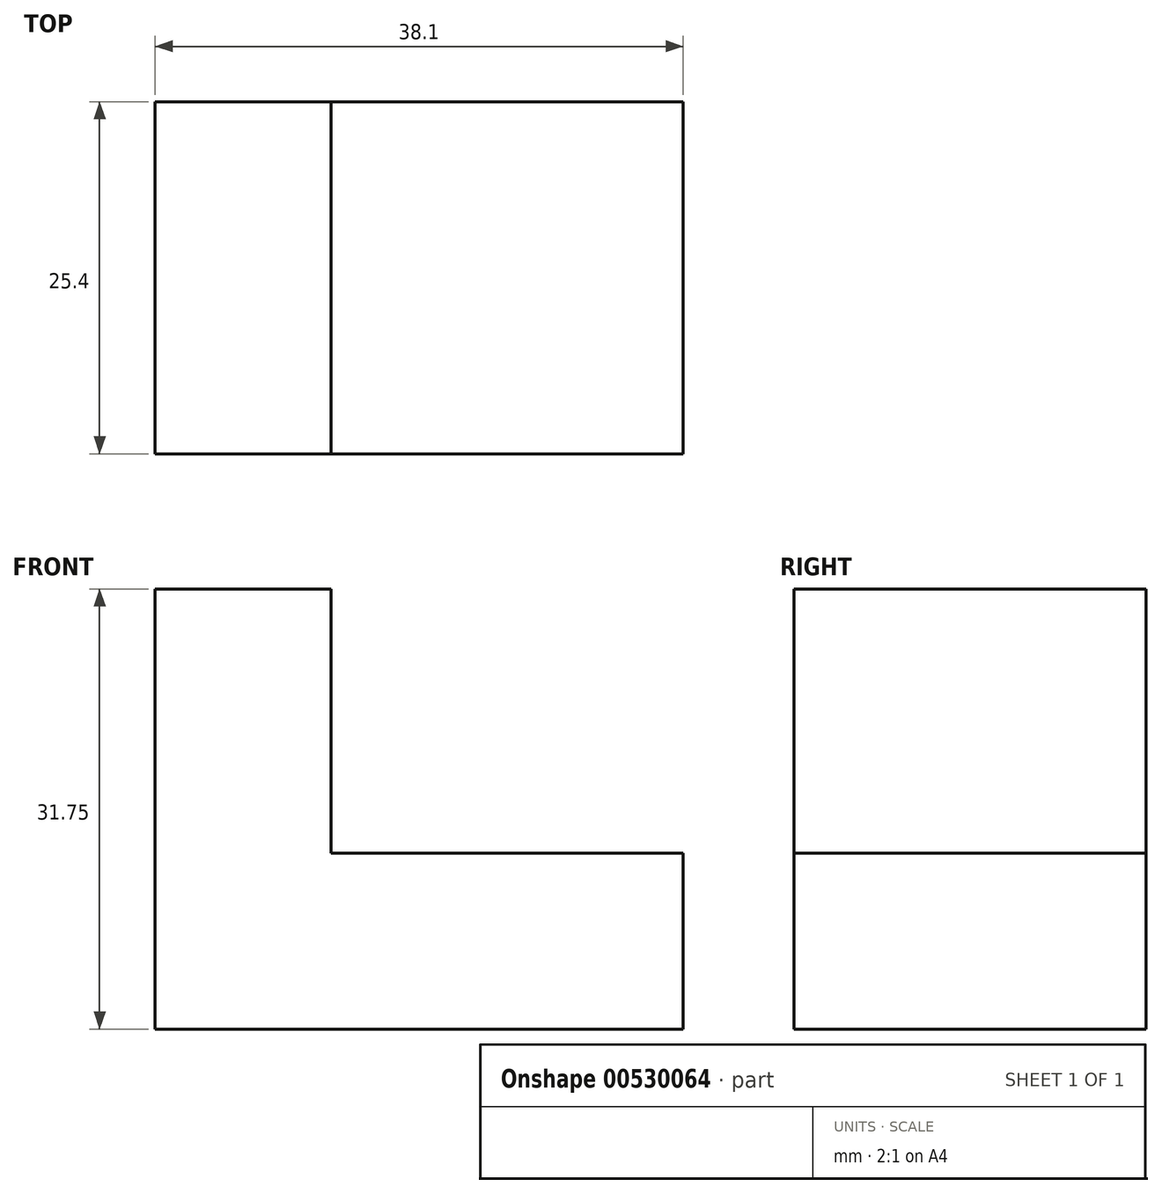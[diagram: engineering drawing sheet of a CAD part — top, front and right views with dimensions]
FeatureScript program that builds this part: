
annotation { "Feature Type Name" : "Feature", "Feature Type Description" : "" }
export const myFeature = defineFeature(function(context is Context, id is Id, definition is map)
    precondition{}
    {
        {
            var Q0;
            Q0=qCreatedBy(makeId("Front.planeOp"),FACE);
            var sketch = newSketch(context, id + "F0", { "sketchPlane" : qUnion([Q0])});
            skLineSegment(sketch, "E0", {"start": v(-58.06, 31.75) * mm, "end": v(-58.06, 0) * mm});
            skLineSegment(sketch, "E1", {"start": v(-58.06, 0) * mm, "end": v(-19.96, 0) * mm});
            skLineSegment(sketch, "E2", {"start": v(-19.96, 0) * mm, "end": v(-19.96, 12.7) * mm});
            skLineSegment(sketch, "E3", {"start": v(-19.96, 12.7) * mm, "end": v(-45.36, 12.7) * mm});
            skLineSegment(sketch, "E4", {"start": v(-45.36, 12.7) * mm, "end": v(-45.36, 31.75) * mm});
            skLineSegment(sketch, "E5", {"start": v(-58.06, 31.75) * mm, "end": v(-45.36, 31.75) * mm});
            skSolve(sketch);
        }
        {
            var Q0;
            Q0 = qSketchRegion(id + "F0", true);
            extrude(context, id + "F1", {"entities" : qUnion([Q0]), "depth" : 25.4 * mm, "offsetDistance" : 25.4 * mm});
        }
    });
